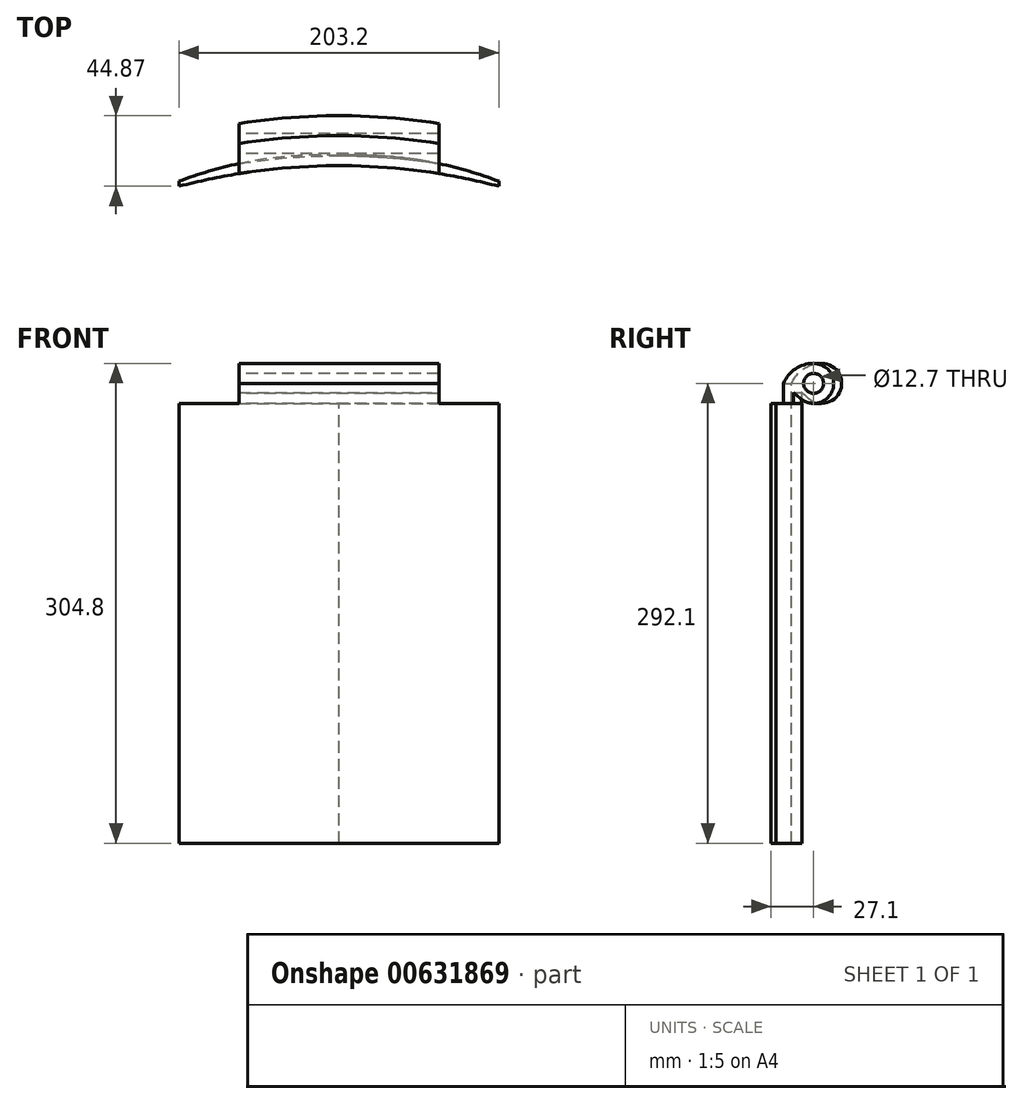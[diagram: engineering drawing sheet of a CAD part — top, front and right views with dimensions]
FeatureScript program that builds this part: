
annotation { "Feature Type Name" : "Feature", "Feature Type Description" : "" }
export const myFeature = defineFeature(function(context is Context, id is Id, definition is map)
    precondition{}
    {
        {
            var Q0;
            Q0=qCreatedBy(makeId("Top.planeOp"),FACE);
            var sketch = newSketch(context, id + "F0", { "sketchPlane" : qUnion([Q0])});
            skLineSegment(sketch, "E0", {"start": v(0, 0) * mm, "end": v(0, 25.4) * mm});
            skArc(sketch, "E1", {"start": v(63.5, -5.08) * mm, "mid": v(0, 0) * mm, "end": v(-63.5, -5.08) * mm});
            skLineSegment(sketch, "E2", {"start": v(0, 25.4) * mm, "end": v(-63.5, 25.4) * mm});
            skLineSegment(sketch, "E3", {"start": v(0, 25.4) * mm, "end": v(63.5, 25.4) * mm});
            skLineSegment(sketch, "E4", {"start": v(63.5, 25.4) * mm, "end": v(63.5, -5.08) * mm});
            skLineSegment(sketch, "E5", {"start": v(-63.5, 25.4) * mm, "end": v(-63.5, -5.08) * mm});
            skPoint(sketch, "E6.start.orphan", {"position": v(-139.7, 0) * mm});
            skPoint(sketch, "E7.start.orphan", {"position": v(139.7, 0) * mm});
            skSolve(sketch);
        }
        {
            var Q0;
            Q0=qCreatedBy(makeId("Right.planeOp"),FACE);
            cPlane(context, id + "F1", {"entities" : qUnion([Q0]), "cplaneType" : CPlaneType.OFFSET, "offset" : 63.5 * mm, "oppositeDirection" : true, "width" : 152.4 * mm, "height" : 152.4 * mm});
        }
        {
            var Q0;
            Q0=qCreatedBy(id+"F1.planeOp",FACE);
            var sketch = newSketch(context, id + "F2", { "sketchPlane" : qUnion([Q0])});
            skArc(sketch, "E8", {"start": v(4.23, -9.47) * mm, "mid": v(24.56, -4.53) * mm, "end": v(12.7, 12.7) * mm});
            skPoint(sketch, "E9.endSnap0", {"position": v(6.35, 0) * mm});
            skLineSegment(sketch, "E10", {"start": v(0, -5.68) * mm, "end": v(4.23, -9.47) * mm});
            skLineSegment(sketch, "E11", {"start": v(-6.35, 0) * mm, "end": v(-6.35, -12.7) * mm});
            skLineSegment(sketch, "E12", {"start": v(0, -12.7) * mm, "end": v(0, -5.68) * mm});
            skPoint(sketch, "E9.start.orphan", {"position": v(25.4, 0) * mm});
            skPoint(sketch, "E13.trimOffspring.start.orphan", {"position": v(0, 0) * mm});
            skLineSegment(sketch, "E14", {"start": v(0, -12.7) * mm, "end": v(-6.35, -12.7) * mm});
            skPoint(sketch, "E15.end.orphan", {"position": v(0, -25.4) * mm});
            skPoint(sketch, "E16.orphan", {"position": v(-6.35, -25.4) * mm});
            skArc(sketch, "E17", {"start": v(12.7, 12.7) * mm, "mid": v(1.22, 9.29) * mm, "end": v(-6.35, 0) * mm});
            skSolve(sketch);
        }
        {
            var Q0;
            Q0 = qSketchRegion(id + "F2", true);
            var Q1;
            Q1=sQuery(id+"F0.wireOp",EDGE,"E1");
            sweep(context, id + "F3", {"profiles" : qUnion([Q0]), "path" : qUnion([Q1]), "keepProfileOrientation" : true});
        }
        {
            var Q0;
            Q0=qCreatedBy(makeId("Right.planeOp"),FACE);
            cPlane(context, id + "F4", {"entities" : qUnion([Q0]), "cplaneType" : CPlaneType.OFFSET, "offset" : 63.5 * mm, "width" : 152.4 * mm, "height" : 152.4 * mm});
        }
        {
            var Q0;
            Q0=qCreatedBy(id+"F4.planeOp",FACE);
            var sketch = newSketch(context, id + "F5", { "sketchPlane" : qUnion([Q0])});
            skCircle(sketch, "E18", {"center": v(0, 0) * mm, "radius": 50.3 * mm});
            skSolve(sketch);
        }
        {
            var Q0;
            Q0 = qSketchRegion(id + "F5", true);
            extrude(context, id + "F6", {"entities" : qUnion([Q0]), "operationType" : NewBodyOperationType.REMOVE, "depth" : 25.4 * mm, "offsetDistance" : 25.4 * mm});
        }
        {
            var Q0;
            Q0=makeQuery(id+"F3.opSweep","CAP_FACE",FACE,{"disambiguationData":[OSD([sQuery(id+"F0.wireOp",VERTEX,"E1.end"),sQuery(id+"F2.wireOp",EDGE,"E8"),sQuery(id+"F2.wireOp",EDGE,"E10"),sQuery(id+"F2.wireOp",EDGE,"E11"),sQuery(id+"F2.wireOp",EDGE,"E12"),sQuery(id+"F2.wireOp",EDGE,"E14"),sQuery(id+"F2.wireOp",EDGE,"TbiANnX9-tqTe-qDmA-Iu70-x5uAycqzRGhP")])],"isStart":true});
            var sketch = newSketch(context, id + "F7", { "sketchPlane" : qUnion([Q0])});
            skCircle(sketch, "E19", {"center": v(-12.7, 0) * mm, "radius": 6.35 * mm});
            skSolve(sketch);
        }
        {
            var Q0;
            Q0 = qSketchRegion(id + "F7", true);
            extrude(context, id + "F8", {"entities" : qUnion([Q0]), "operationType" : NewBodyOperationType.REMOVE, "oppositeDirection" : true, "depth" : 127 * mm, "offsetDistance" : 25.4 * mm});
        }
        {
            var Q0;
            Q0=makeQuery(id+"F3.opSweep","SWEPT_FACE",FACE,{"disambiguationData":[OSD([sQuery(id+"F0.wireOp",EDGE,"E1"),sQuery(id+"F2.wireOp",EDGE,"E14")])]});
            var sketch = newSketch(context, id + "F9", { "sketchPlane" : qUnion([Q0])});
            skLineSegment(sketch, "E20", {"start": v(-101.6, 11.23) * mm, "end": v(-101.6, 14.04) * mm});
            skLineSegment(sketch, "E21", {"start": v(101.6, 11.23) * mm, "end": v(101.6, 14.4) * mm});
            skArc(sketch, "E22", {"start": v(-101.6, 14.4) * mm, "mid": v(-51.22, 4.57) * mm, "end": v(0, 1.28) * mm});
            skArc(sketch, "E23", {"start": v(0, 1.28) * mm, "mid": v(51.22, 4.57) * mm, "end": v(101.6, 14.4) * mm});
            skLineSegment(sketch, "E24", {"start": v(-101.6, 14.4) * mm, "end": v(-101.6, 11.23) * mm});
            skArc(sketch, "E25", {"start": v(0, -5.07) * mm, "mid": v(51.65, -2.2) * mm, "end": v(101.6, 11.23) * mm});
            skArc(sketch, "E26", {"start": v(-101.6, 11.23) * mm, "mid": v(-51.65, -2.2) * mm, "end": v(0, -5.07) * mm});
            skPoint(sketch, "E27.orphan", {"position": v(-101.6, 0) * mm});
            skPoint(sketch, "E28.orphan", {"position": v(101.6, 0) * mm});
            skSolve(sketch);
        }
        {
            var Q0;
            Q0 = qSketchRegion(id + "F9", true);
            extrude(context, id + "F10", {"entities" : qUnion([Q0]), "operationType" : NewBodyOperationType.ADD, "depth" : 279.4 * mm, "offsetDistance" : 25.4 * mm});
        }
    });
